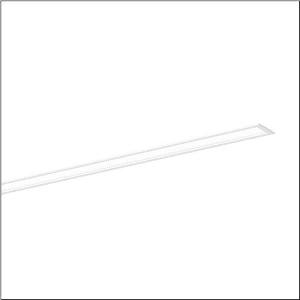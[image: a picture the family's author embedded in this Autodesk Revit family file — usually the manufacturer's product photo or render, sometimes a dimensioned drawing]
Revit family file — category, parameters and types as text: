
# Revit family: silica_21_51mx13dh31wb
name_source: partatom
category: Lighting Fixtures
units: mm (PartAtom-declared; Revit-internal decimal feet)

## family parameters
Cut with Voids When Loaded = No
Host = Face
Light Source = No
Part Type = Normal
Room Calculation Point = No
Round Connector Dimension = Use Diameter
Shared = No

## types (1)
- --- (1 x LED, 1640 lm, 13.8 W, 3000K)
    Apparent Load = 14 VA
    CIE Flux Codes = 78 96 99 100 100
    Color Rendering = 80
    Color Temperature = 3000K
    Default Elevation = 1800 mm
    Description = Silica 21, office luminaire, primary optical cover: prismatic diffuser, of PMMA, CAT 2 (L<= 3000cd/m²), light emission: direct distribution, primary light characteristic: symmetric, installation type: recessed, LED, rated luminous flux: 1.640lm, luminous efficacy: 119lm/W, light colour: 830, colour temperature: 3000K, control gear: DALI 2, with terminal, 3+2-pole, max. 2.5mm², mains connection: 220..240V, AC, 50/60Hz, rated input power: 13.8W, luminaire housing, of aluminium, traffic white (RAL 9016), length: 628mm, width: 79mm, height: 53mm, protection rating (complete): IP20, insulation class (complete): insulation class I (protective earthing), certification: CE, permissible operating ambient temperature: 0..+35°C, standard: EN 50419, packaging unit: 1 piece
    Height = 0 mm  [stored 0 ft]
    Lamp = 1 x LED
    Lamp Light Flux = 1640 lm
    Lamp Power = 13.8 W
    Lamp count = 1
    Length = 627 mm
    Luminous efficacy = 119 lm/W
    Manufacturer = Siteco
    ModVariant = No
    Model = 51MX13DH31WB
    Mounting Place = Ceiling
    Mounting Type = Recessed
    Number of Poles = 1
    OnlyDefault = Yes
    Power Factor = 1
    Product Name = Silica 21
    Product group = office luminaire | ceiling recessed
    ProductGroupID = 400
    Protection Class = Protection class I
    Protection Degree = IP 20
    RLX_Detail_Level = 1
    RLX_Emergency_Light_Flux = 0 lm
    RLX_Emergency_Type = 0
    RLX_Emergency_Type_DB = No
    RlxData = <blob elided: 14449 chars, md5=36a6b492>
    Socket = socket
    Standby Power = 0 W
    System Light Flux = 1640 lm
    System Power = 14 W
    Type Comments = factory setting: luminous flux: 100 % | dim-lin: 254 | 170 mA
    Type Image = l_1335881.jpg
    URL = http://relux.com
    VarID = @adj_031043
    Voltage = 0 V
    Weight = 0.00 kg
    Width = 79 mm

note: [stored X ft] marks values corroborated as IEEE doubles in the binary element streams (Revit-internal decimal feet)

## geometry (parser evidence)
native form markers: Sweep x12
no freeform markers — native parametric forms only
